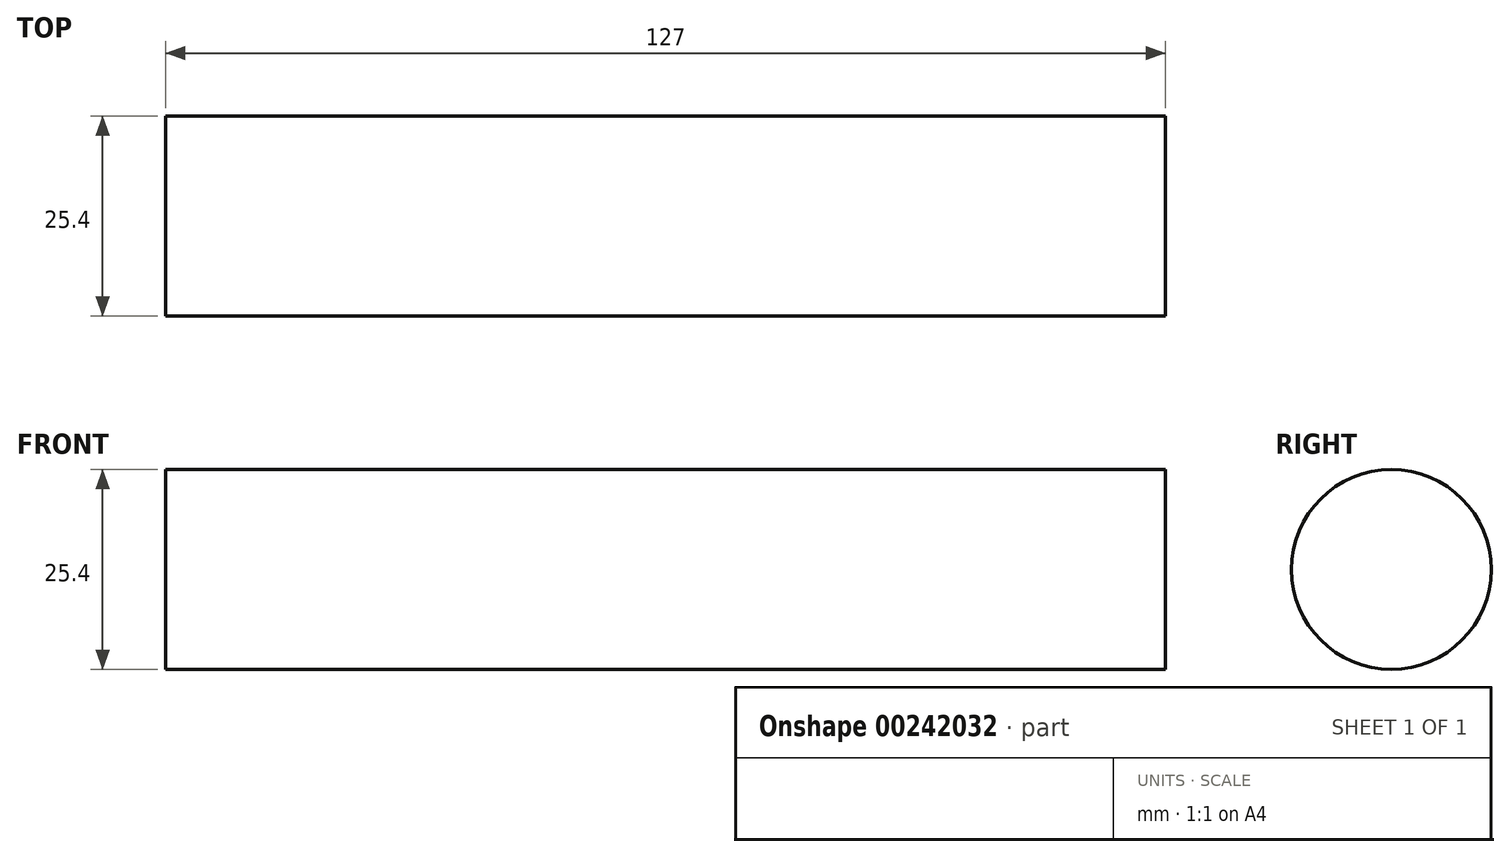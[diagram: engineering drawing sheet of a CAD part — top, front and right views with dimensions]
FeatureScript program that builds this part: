
annotation { "Feature Type Name" : "Feature", "Feature Type Description" : "" }
export const myFeature = defineFeature(function(context is Context, id is Id, definition is map)
    precondition{}
    {
        {
            var Q0;
            Q0=qCreatedBy(makeId("Right.planeOp"),FACE);
            var sketch = newSketch(context, id + "F0", { "sketchPlane" : qUnion([Q0])});
            skCircle(sketch, "E0", {"center": v(0, 0) * mm, "radius": 12.7 * mm});
            skSolve(sketch);
        }
        {
            var Q0;
            Q0 = qSketchRegion(id + "F0", true);
            extrude(context, id + "F1", {"entities" : qUnion([Q0]), "depth" : 127 * mm});
        }
    });
